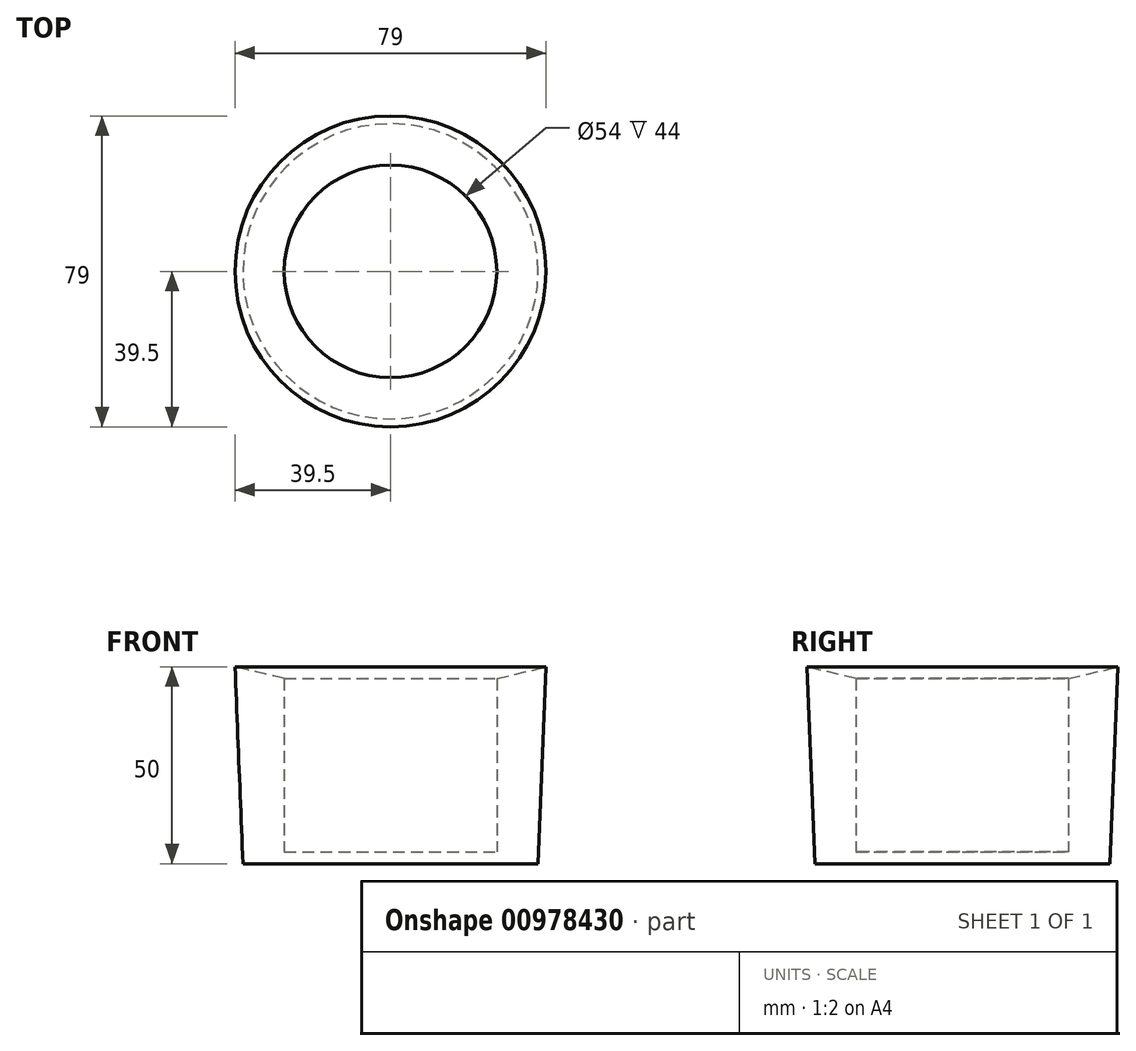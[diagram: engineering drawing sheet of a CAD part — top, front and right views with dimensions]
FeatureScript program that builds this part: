
annotation { "Feature Type Name" : "Feature", "Feature Type Description" : "" }
export const myFeature = defineFeature(function(context is Context, id is Id, definition is map)
    precondition{}
    {
        {
            var Q0;
            Q0=qCreatedBy(makeId("Front.planeOp"),FACE);
            var sketch = newSketch(context, id + "F0", { "sketchPlane" : qUnion([Q0])});
            skLineSegment(sketch, "E0", {"start": v(0, 0) * mm, "end": v(-27, 0) * mm});
            skLineSegment(sketch, "E1", {"start": v(-27, 0) * mm, "end": v(-27, 44) * mm});
            skLineSegment(sketch, "E2", {"start": v(-27, 44) * mm, "end": v(-39.5, 47) * mm});
            skLineSegment(sketch, "E3", {"start": v(-39.5, 47) * mm, "end": v(-37.5, -3) * mm});
            skLineSegment(sketch, "E4", {"start": v(-37.5, -3) * mm, "end": v(0, -3) * mm});
            skLineSegment(sketch, "E5", {"start": v(0, -3) * mm, "end": v(0, 0) * mm});
            skSolve(sketch);
        }
        {
            var Q0;
            Q0=makeQuery(id+"F0.imprint","IMPRINT",FACE,{"disambiguationData":[TD([[makeQuery(id+"F0.imprint","IMPRINT",EDGE,{"derivedFrom":sQuery(id+"F0.wireOp",EDGE,"E0")}),1.0]])]});
            var Q1;
            Q1=sQuery(id+"F0.wireOp",EDGE,"E5");
            revolve(context, id + "F1", {"surfaceOperationType" : NewSurfaceOperationType.NEW, "entities" : qUnion([Q0]), "axis" : qUnion([Q1]), "revolveType" : RevolveType.FULL});
        }
    });
